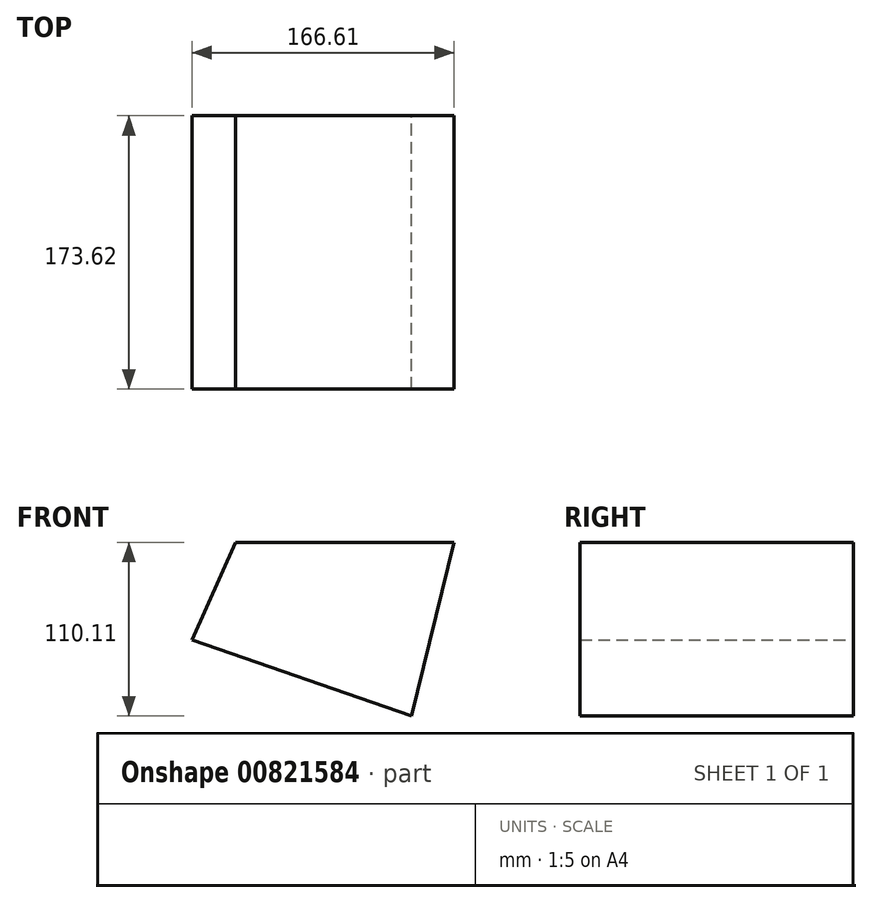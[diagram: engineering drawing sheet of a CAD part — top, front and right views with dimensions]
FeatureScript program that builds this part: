
annotation { "Feature Type Name" : "Feature", "Feature Type Description" : "" }
export const myFeature = defineFeature(function(context is Context, id is Id, definition is map)
    precondition{}
    {
        {
            var Q0;
            Q0=qCreatedBy(makeId("Front.planeOp"),FACE);
            var sketch = newSketch(context, id + "F0", { "sketchPlane" : qUnion([Q0])});
            skLineSegment(sketch, "E0", {"start": v(-62.35, 38.37) * mm, "end": v(76.6, 38.37) * mm});
            skLineSegment(sketch, "E1", {"start": v(76.6, 38.37) * mm, "end": v(49.45, -71.74) * mm});
            skLineSegment(sketch, "E2", {"start": v(49.45, -71.74) * mm, "end": v(-90.02, -23.42) * mm});
            skLineSegment(sketch, "E3", {"start": v(-90.02, -23.42) * mm, "end": v(-62.35, 38.37) * mm});
            skSolve(sketch);
        }
        {
            var Q0;
            Q0=makeQuery(id+"F0.imprint","IMPRINT",FACE,{"disambiguationData":[TD([[makeQuery(id+"F0.imprint","IMPRINT",EDGE,{"derivedFrom":sQuery(id+"F0.wireOp",EDGE,"E0")}),-1.0]])]});
            extrude(context, id + "F1", {"entities" : qUnion([Q0]), "endBound" : BoundingType.SYMMETRIC, "depth" : 173.63 * mm, "offsetDistance" : 25.4 * mm});
        }
    });
